# Revit family: NXPBAR
name_source: partatom
category: Communication Devices
revit_build: Autodesk Revit 2014 (Build: 20130308_1515(x64)
units: mm (PartAtom-declared; Revit-internal decimal feet)

## types (1)
- NXPBAR
    Assembly Code = D5090
    Default Elevation = 48 "
    Description = The Hubbell Control Solutions NX Relay Channel Barrier provides
a code gauge steel separation between any two relays in the NX
lighting control panel. This facilitates the code required isolation
of relays controlling emergency circuits from relays controlling
normal lighting circuits. The NXPBAR can be used to section
off part of a high voltage relay channel in a NX panel for other
requirements as well. The optional barriers are ordered separately
in pairs for field installation.
    Features = Field installed
• Code gauge steel construction
• Installs between any two relays
• Complies with emergency circuit requirements
• Universal fit, left or right side of NX Lighting Control panel
• Five year limited warranty
    Manufacturer = Hubbell Control Solutions
    Material = Plastic - Hubbell - Gray
    Model = Lighting Control Panel Relay Channel Barrier
    Product Documentation Link = https://hubbellcdn.com
    Product Page URL = https://www.hubbell.com
    Type Comments = Lighting Control Panel Relay Channel Barrier
    URL = https://www.hubbell.com
    Warranty = 5-Years Warranty

## geometry (parser evidence)
native form markers: Sweep x1
no freeform markers — native parametric forms only
